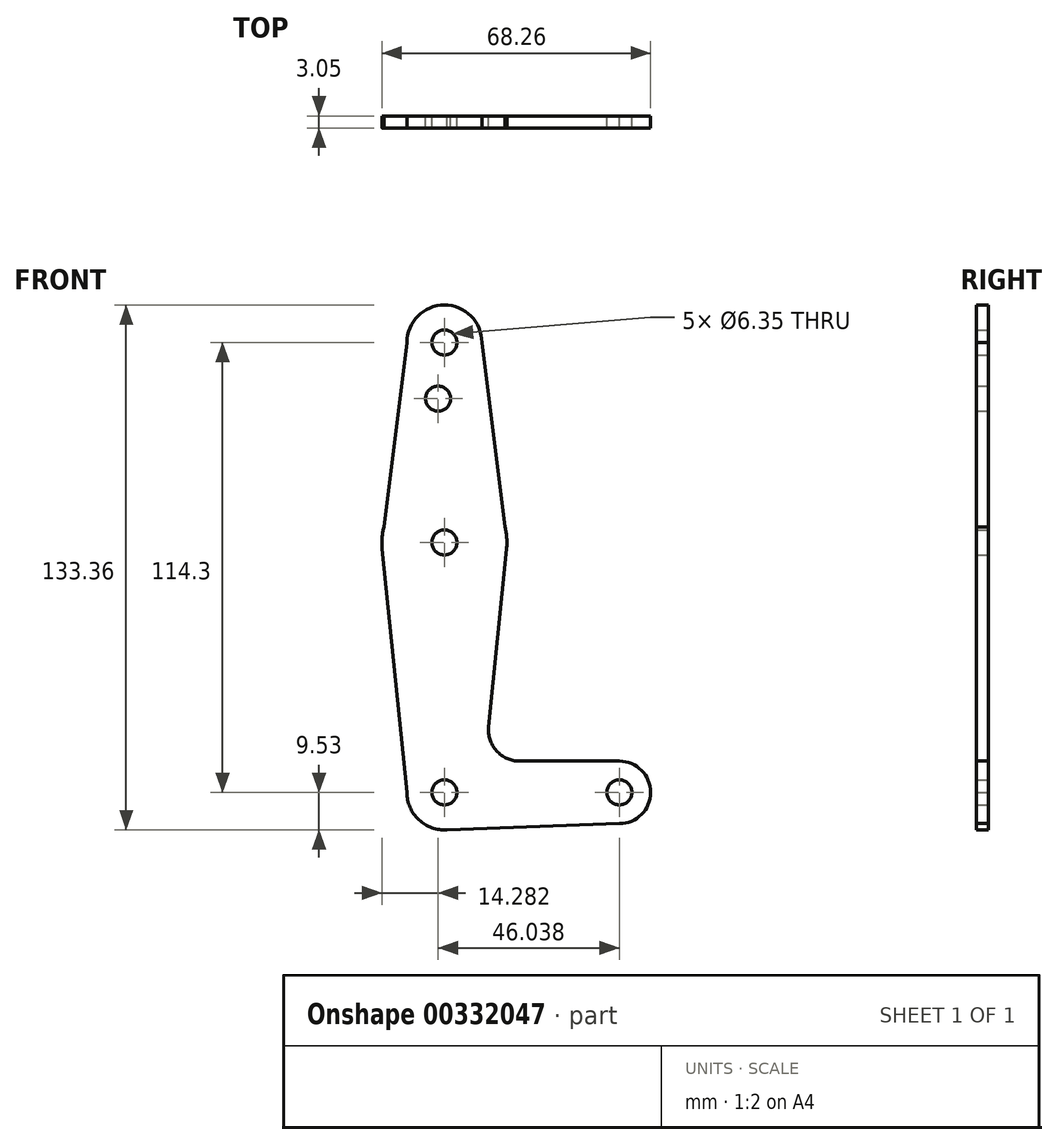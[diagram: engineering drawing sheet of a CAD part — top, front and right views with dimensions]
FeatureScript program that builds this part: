
annotation { "Feature Type Name" : "Feature", "Feature Type Description" : "" }
export const myFeature = defineFeature(function(context is Context, id is Id, definition is map)
    precondition{}
    {
        {
            var Q0;
            Q0=qCreatedBy(makeId("Front.planeOp"),FACE);
            var sketch = newSketch(context, id + "F0", { "sketchPlane" : qUnion([Q0])});
            skLineSegment(sketch, "E0", {"start": v(0, 0) * mm, "end": v(0, 114.3) * mm, "construction": true});
            skLineSegment(sketch, "E1", {"start": v(0, 0) * mm, "end": v(44.45, 0) * mm, "construction": true});
            skCircle(sketch, "E2", {"center": v(0, 0) * mm, "radius": 9.53 * mm});
            skCircle(sketch, "E3", {"center": v(44.45, 0) * mm, "radius": 7.94 * mm});
            skCircle(sketch, "E4", {"center": v(0, 63.5) * mm, "radius": 15.88 * mm});
            skCircle(sketch, "E5", {"center": v(0, 114.3) * mm, "radius": 9.53 * mm});
            skLineSegment(sketch, "E6", {"start": v(-9.52, 114.3) * mm, "end": v(-15.88, 63.5) * mm});
            skLineSegment(sketch, "E7", {"start": v(9.52, 114.3) * mm, "end": v(15.88, 63.5) * mm});
            skLineSegment(sketch, "E8", {"start": v(-9.53, 0) * mm, "end": v(-15.8, 61.9) * mm});
            skLineSegment(sketch, "E9", {"start": v(11.22, 16.69) * mm, "end": v(15.8, 61.9) * mm});
            skLineSegment(sketch, "E10", {"start": v(19.12, 7.94) * mm, "end": v(44.45, 7.94) * mm});
            skLineSegment(sketch, "E11", {"start": v(0, -9.52) * mm, "end": v(44.45, -7.94) * mm});
            skCircle(sketch, "E12", {"center": v(0, 114.3) * mm, "radius": 3.18 * mm});
            skCircle(sketch, "E13", {"center": v(0, 63.5) * mm, "radius": 3.18 * mm});
            skCircle(sketch, "E14", {"center": v(44.45, 0) * mm, "radius": 3.18 * mm});
            skCircle(sketch, "E15", {"center": v(0, 0) * mm, "radius": 3.18 * mm});
            skCircle(sketch, "E16", {"center": v(-1.59, 100.03) * mm, "radius": 3.18 * mm});
            skArc(sketch, "E17.filletArc", {"start": v(11.22, 16.69) * mm, "mid": v(13.23, 10.56) * mm, "end": v(19.12, 7.94) * mm});
            skSolve(sketch);
        }
        {
            var Q0;
            Q0 = qSketchRegion(id + "F0", true);
            extrude(context, id + "F1", {"entities" : qUnion([Q0]), "depth" : 3.05 * mm});
        }
    });
